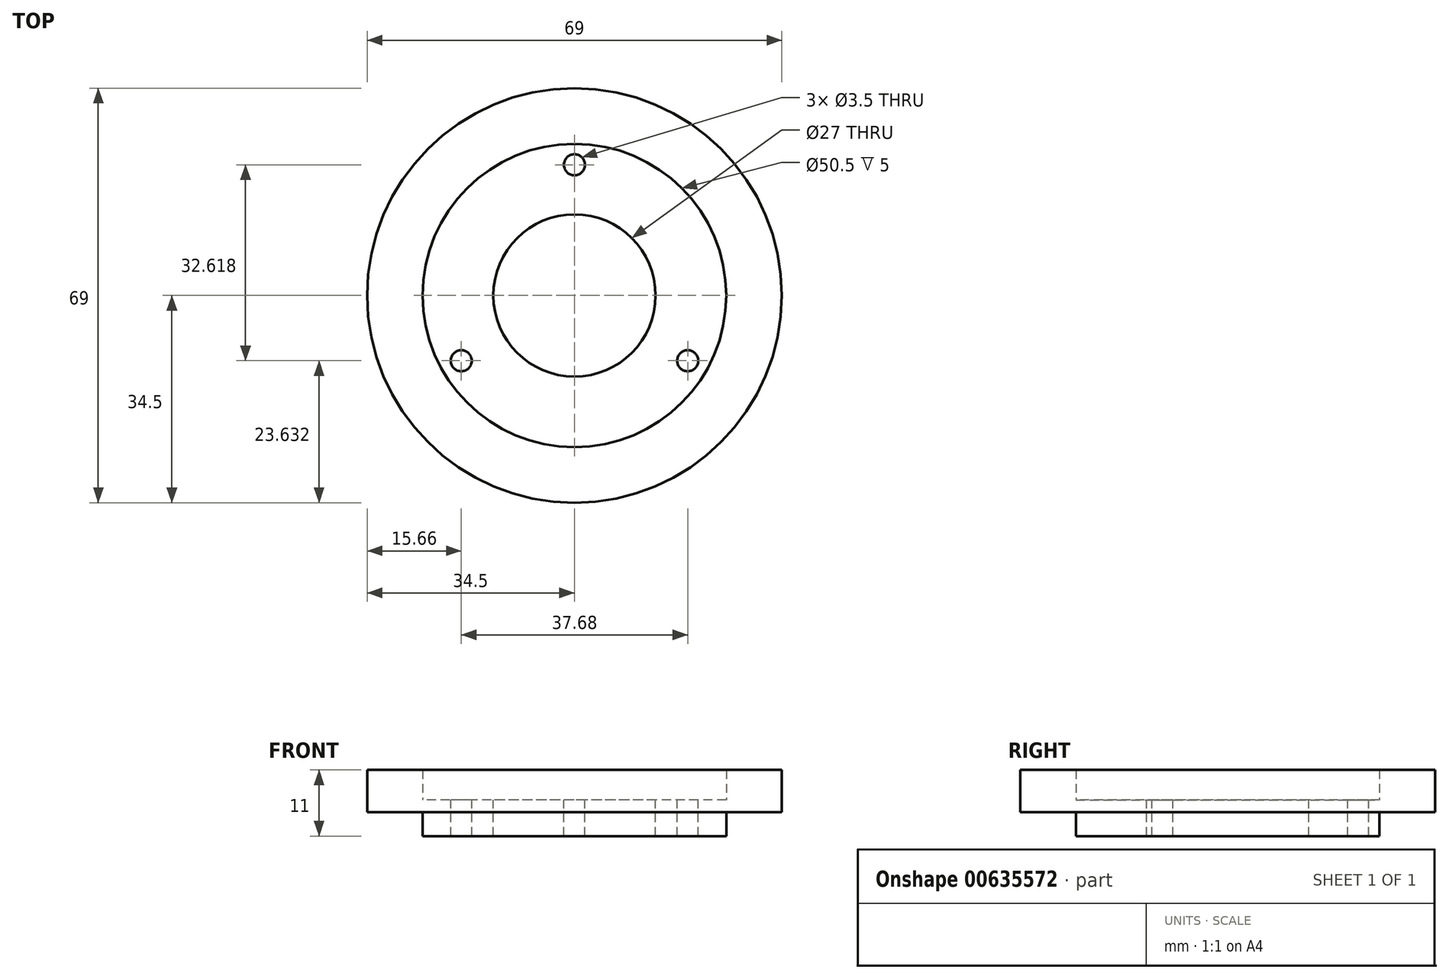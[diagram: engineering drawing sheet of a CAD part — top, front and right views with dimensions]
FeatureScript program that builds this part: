
annotation { "Feature Type Name" : "Feature", "Feature Type Description" : "" }
export const myFeature = defineFeature(function(context is Context, id is Id, definition is map)
    precondition{}
    {
        {
            var Q0;
            Q0=qCreatedBy(makeId("Top.planeOp"),FACE);
            var sketch = newSketch(context, id + "F0", { "sketchPlane" : qUnion([Q0])});
            skCircle(sketch, "E0", {"center": v(0, 0) * mm, "radius": 34.5 * mm});
            skCircle(sketch, "E1", {"center": v(0, 0) * mm, "radius": 13.5 * mm});
            skCircle(sketch, "E2", {"center": v(0, 0) * mm, "radius": 12.5 * mm});
            skCircle(sketch, "E3", {"center": v(0, 0) * mm, "radius": 25.25 * mm});
            skCircle(sketch, "E4", {"center": v(0, 21.75) * mm, "radius": 1.75 * mm});
            skCircle(sketch, "E5", {"center": v(-18.84, -10.87) * mm, "radius": 1.75 * mm});
            skCircle(sketch, "E6", {"center": v(18.84, -10.87) * mm, "radius": 1.75 * mm});
            skSolve(sketch);
        }
        {
            var Q0;
            Q0=makeQuery(id+"F0.imprint","IMPRINT",FACE,{"disambiguationData":[TD([[makeQuery(id+"F0.imprint","IMPRINT",EDGE,{"derivedFrom":sQuery(id+"F0.wireOp",EDGE,"E1")}),-1.0]])]});
            var Q1;
            Q1=sQuery(id+"F0.wireOp",EDGE,"E3");
            var Q2;
            Q2=sQuery(id+"F0.wireOp",EDGE,"E1");
            var Q3;
            Q3=sQuery(id+"F0.wireOp",EDGE,"E4");
            var Q4;
            Q4=sQuery(id+"F0.wireOp",EDGE,"E5");
            var Q5;
            Q5=sQuery(id+"F0.wireOp",EDGE,"E6");
            extrude(context, id + "F1", {"entities" : qUnion([Q0]), "surfaceEntities" : qUnion([Q1, Q2, Q3, Q4, Q5]), "oppositeDirection" : true, "depth" : 4 * mm, "offsetDistance" : 25.4 * mm});
        }
        {
            var Q0;
            Q0 = qSketchRegion(id + "F0", true);
            var Q1;
            Q1=makeQuery(id+"F1.opExtrude","CAP_FACE",FACE,{"disambiguationData":[OSD([sQuery(id+"F0.wireOp",EDGE,"E1"),sQuery(id+"F0.wireOp",EDGE,"E3"),sQuery(id+"F0.wireOp",EDGE,"E4"),sQuery(id+"F0.wireOp",EDGE,"E5"),sQuery(id+"F0.wireOp",EDGE,"E6")])],"isStart":true});
            extrude(context, id + "F2", {"entities" : qUnion([Q0, Q1]), "operationType" : NewBodyOperationType.ADD, "depth" : 2 * mm, "offsetDistance" : 25.4 * mm});
        }
        {
            var Q0;
            Q0=makeQuery(id+"F0.imprint","IMPRINT",FACE,{"disambiguationData":[TD([[makeQuery(id+"F0.imprint","IMPRINT",EDGE,{"derivedFrom":sQuery(id+"F0.wireOp",EDGE,"E0")}),1.0]])]});
            extrude(context, id + "F3", {"entities" : qUnion([Q0]), "operationType" : NewBodyOperationType.ADD, "depth" : 7 * mm, "offsetDistance" : 25.4 * mm});
        }
    });
